FCSTD DOCUMENT  (FreeCAD 0.18R14220 (Git))
Label: sketch_objectsFV7g6h
License: All rights reserved
LicenseURL: http://en.wikipedia.org/wiki/All_rights_reserved
objects: Sketcher::SketchObject×1
note: 1 computed .brp shape members not serialized (recipe doc carries the construction recipe); baked Part::Feature solids carry a one-line shape summary decoded from their .brp

FEATURE [Sketcher::SketchObject] Sketch_sketch_objects
  sketch-geometry (52):
    g0: ArcOfEllipse CenterX=49.7013 CenterY=238.606 CenterZ=0 NormalX=0 NormalY=0 NormalZ=1 MajorRadius=43.2012 MinorRadius=14.2179 AngleXU=-0.622367 StartAngle=5.79407 EndAngle=11.4202
    g1: LineSegment StartX=76.7923 StartY=210.947 StartZ=0 EndX=49.7013 EndY=238.606 EndZ=0
    g2: LineSegment StartX=49.7013 StartY=238.606 StartZ=0 EndX=56.6103 EndY=217.704 EndZ=0
    g3: LineSegment [constr] StartX=41.1792 StartY=270.878 StartZ=0 EndX=41.2353 EndY=287.037 EndZ=0
    g4: LineSegment [constr] StartX=41.2353 StartY=287.037 StartZ=0 EndX=49.7121 EndY=279.07 EndZ=0
    g5: LineSegment [constr] StartX=49.7121 StartY=279.07 StartZ=0 EndX=49.656 EndY=262.912 EndZ=0
    g6: LineSegment [constr] StartX=49.656 StartY=262.912 StartZ=0 EndX=41.1792 EndY=270.878 EndZ=0
    g7: LineSegment [constr] StartX=41.1926 StartY=274.753 StartZ=0 EndX=42.6528 EndY=273.38 EndZ=0
    g8: LineSegment [constr] StartX=42.6528 StartY=273.38 StartZ=0 EndX=42.6393 EndY=269.506 EndZ=0
    g9: LineSegment [constr] StartX=41.2218 StartY=283.163 StartZ=0 EndX=42.682 EndY=281.79 EndZ=0
    g10: LineSegment [constr] StartX=42.682 StartY=281.79 StartZ=0 EndX=42.6954 EndY=285.665 EndZ=0
    g11: LineSegment [constr] StartX=49.6987 StartY=275.196 StartZ=0 EndX=48.2385 EndY=276.568 EndZ=0
    g12: LineSegment [constr] StartX=48.2385 StartY=276.568 StartZ=0 EndX=48.252 EndY=280.442 EndZ=0
    g13: LineSegment [constr] StartX=49.6695 StartY=266.786 StartZ=0 EndX=48.2093 EndY=268.158 EndZ=0
    g14: LineSegment [constr] StartX=48.2093 StartY=268.158 StartZ=0 EndX=48.1959 EndY=264.284 EndZ=0
    g15: LineSegment StartX=41.1919 StartY=274.677 StartZ=0 EndX=41.1332 EndY=283.085 EndZ=0
    g16: LineSegment StartX=42.5821 StartY=285.717 StartZ=0 EndX=48.3338 EndY=280.577 EndZ=0
    g17: LineSegment StartX=49.5946 StartY=276.745 StartZ=0 EndX=49.9588 EndY=268.335 EndZ=0
    g18: LineSegment StartX=48.6946 StartY=264.078 StartZ=0 EndX=42.6645 EndY=269.5 EndZ=0
    g19: ArcOfEllipse CenterX=42.6449 CenterY=273.391 CenterZ=0 NormalX=0 NormalY=0 NormalZ=-1 MajorRadius=4.13656 MinorRadius=1.36086 AngleXU=1.43988 StartAngle=3.50878 EndAngle=5.07438
    g20: ArcOfEllipse CenterX=42.5838 CenterY=281.856 CenterZ=0 NormalX=0 NormalY=0 NormalZ=-1 MajorRadius=4.10185 MinorRadius=1.36491 AngleXU=1.44326 StartAngle=5.06155 EndAngle=6.64982
    g21: ArcOfEllipse CenterX=47.7793 CenterY=276.567 CenterZ=0 NormalX=0 NormalY=0 NormalZ=-1 MajorRadius=4.30289 MinorRadius=1.82063 AngleXU=1.53942 StartAngle=0.382777 EndAngle=1.54265
    g22: ArcOfEllipse CenterX=48.8554 CenterY=268.083 CenterZ=0 NormalX=0 NormalY=0 NormalZ=-1 MajorRadius=4.12784 MinorRadius=1.11184 AngleXU=1.54193 StartAngle=1.51729 EndAngle=3.39278
    g23: LineSegment StartX=63.7123 StartY=263.806 StartZ=0 EndX=55.9428 EndY=260.556 EndZ=0
    g24: LineSegment StartX=55.9428 StartY=260.556 StartZ=0 EndX=49.7121 EndY=266.499 EndZ=0
    g25: LineSegment StartX=49.7121 StartY=266.499 StartZ=0 EndX=49.7121 EndY=277.16 EndZ=0
    g26: LineSegment StartX=49.7121 StartY=277.16 StartZ=0 EndX=55.9428 EndY=284.511 EndZ=0
    g27: LineSegment StartX=55.9428 StartY=284.511 StartZ=0 EndX=63.7123 EndY=283.017 EndZ=0
    g28: LineSegment StartX=63.7123 StartY=283.017 StartZ=0 EndX=67.17 EndY=273.802 EndZ=0
    g29: LineSegment StartX=67.17 StartY=273.802 StartZ=0 EndX=63.7123 EndY=263.806 EndZ=0
    g30: LineSegment StartX=38.4028 StartY=255.231 StartZ=0 EndX=49.656 EndY=262.912 EndZ=0
    g31: LineSegment StartX=49.656 StartY=262.912 StartZ=0 EndX=49.7121 EndY=253.933 EndZ=0
    g32: LineSegment StartX=49.7121 StartY=253.933 StartZ=0 EndX=60.2819 EndY=256.396 EndZ=0
    g33: BSplineCurve PolesCount=4 KnotsCount=2 Degree=3 IsPeriodic=0
    g34: Circle [constr] CenterX=49.7121 CenterY=300.956 CenterZ=0 NormalX=0 NormalY=0 NormalZ=1 AngleXU=0 Radius=0.72
    g35: Circle [constr] CenterX=60.1938 CenterY=311.107 CenterZ=0 NormalX=0 NormalY=0 NormalZ=1 AngleXU=0 Radius=0.72
    g36: Circle [constr] CenterX=60.5017 CenterY=302.786 CenterZ=0 NormalX=0 NormalY=0 NormalZ=1 AngleXU=0 Radius=0.72
    g37: BSplineCurve PolesCount=4 KnotsCount=2 Degree=3 IsPeriodic=0
    g38: Circle [constr] CenterX=60.8097 CenterY=294.464 CenterZ=0 NormalX=0 NormalY=0 NormalZ=1 AngleXU=0 Radius=0.72
    g39: Circle [constr] CenterX=58.9652 CenterY=288.321 CenterZ=0 NormalX=0 NormalY=0 NormalZ=1 AngleXU=0 Radius=0.72
    g40: Circle [constr] CenterX=52.8356 CenterY=284.504 CenterZ=0 NormalX=0 NormalY=0 NormalZ=1 AngleXU=0 Radius=0.72
    g41: BSplineCurve PolesCount=4 KnotsCount=2 Degree=3 IsPeriodic=0
    g42: Circle [constr] CenterX=46.7061 CenterY=280.688 CenterZ=0 NormalX=0 NormalY=0 NormalZ=1 AngleXU=0 Radius=0.72
    g43: Circle [constr] CenterX=41.9049 CenterY=288.11 CenterZ=0 NormalX=0 NormalY=0 NormalZ=1 AngleXU=0 Radius=0.72
    g44: Circle [constr] CenterX=47.8785 CenterY=292.399 CenterZ=0 NormalX=0 NormalY=0 NormalZ=1 AngleXU=0 Radius=0.72
    g45: BSplineCurve PolesCount=4 KnotsCount=2 Degree=3 IsPeriodic=0
    g46: Circle [constr] CenterX=53.8521 CenterY=296.689 CenterZ=0 NormalX=0 NormalY=0 NormalZ=1 AngleXU=0 Radius=0.72
    g47: Circle [constr] CenterX=56.7703 CenterY=298.754 CenterZ=0 NormalX=0 NormalY=0 NormalZ=1 AngleXU=0 Radius=0.72
    g48: Circle [constr] CenterX=54.8429 CenterY=293.355 CenterZ=0 NormalX=0 NormalY=0 NormalZ=1 AngleXU=0 Radius=0.72
    g49: BSplineCurve PolesCount=4 KnotsCount=2 Degree=3 IsPeriodic=0
    g50: Circle [constr] CenterX=52.9156 CenterY=287.956 CenterZ=0 NormalX=0 NormalY=0 NormalZ=1 AngleXU=0 Radius=0.72
    g51: Circle [constr] CenterX=49.7121 CenterY=287.987 CenterZ=0 NormalX=0 NormalY=0 NormalZ=1 AngleXU=0 Radius=0.72
  constraints (87):
    c: Coincident(g0,g1)
    c: Coincident(g2,g0)
    c: Coincident(g1,g2)
    c: Coincident(g1,g0)
    c: Coincident(g3,g4)
    c: Coincident(g4,g5)
    c: Coincident(g5,g6)
    c: Coincident(g6,g3)
    c: Coincident(g7,g8)
    c: Coincident(g9,g10)
    c: Coincident(g11,g12)
    c: Coincident(g13,g14)
    c: Equal(g7,g9)
    c: Equal(g7,g11)
    c: Equal(g7,g13)
    c: Equal(g8,g10)
    c: Equal(g8,g12)
    c: Equal(g8,g14)
    c: PointOnObject(g7,g3)
    c: PointOnObject(g8,g6)
    c: PointOnObject(g9,g3)
    c: PointOnObject(g10,g4)
    c: PointOnObject(g11,g5)
    c: PointOnObject(g12,g4)
    c: PointOnObject(g13,g5)
    c: PointOnObject(g14,g6)
    c: Parallel(g3,g5)
    c: Parallel(g3,g8)
    c: Parallel(g3,g10)
    c: Parallel(g3,g12)
    c: Parallel(g3,g14)
    c: Parallel(g4,g6)
    c: Parallel(g4,g7)
    c: Parallel(g4,g9)
    c: Parallel(g4,g11)
    c: Parallel(g4,g13)
    c: Tangent(g19,g15) = 1.5708
    c: Tangent(g15,g20) = 1.5708
    c: Tangent(g20,g16) = 1.5708
    c: Tangent(g16,g21) = 1.5708
    c: Tangent(g21,g17) = 1.5708
    c: Tangent(g17,g22) = 1.5708
    c: Tangent(g22,g18) = 1.5708
    c: Tangent(g18,g19) = 1.5708
    c: Coincident(g23,g24)
    c: Coincident(g24,g25)
    c: Coincident(g25,g26)
    c: Coincident(g26,g27)
    c: Coincident(g27,g28)
    c: Coincident(g28,g29)
    c: Coincident(g29,g23)
    c: Coincident(g30,g31)
    c: Coincident(g31,g32)
    c: Radius(g34) = 0.72
    c: Equal(g35,g34)
    c: Equal(g36,g34)
    c: InternalAlignment(g34,g33)
    c: InternalAlignment(g34,g33)
    c: InternalAlignment(g35,g33)
    c: InternalAlignment(g36,g33)
    c: Equal(g38,g34)
    c: Equal(g39,g34)
    c: Equal(g40,g34)
    c: InternalAlignment(g36,g37)
    c: InternalAlignment(g38,g37)
    c: InternalAlignment(g39,g37)
    c: InternalAlignment(g40,g37)
    c: Equal(g42,g34)
    c: Equal(g43,g34)
    c: Equal(g44,g34)
    c: InternalAlignment(g40,g41)
    c: InternalAlignment(g42,g41)
    c: InternalAlignment(g43,g41)
    c: InternalAlignment(g44,g41)
    c: Equal(g46,g34)
    c: Equal(g47,g34)
    c: Equal(g48,g34)
    c: InternalAlignment(g44,g45)
    c: InternalAlignment(g46,g45)
    c: InternalAlignment(g47,g45)
    c: InternalAlignment(g48,g45)
    c: Equal(g50,g34)
    c: Equal(g51,g34)
    c: InternalAlignment(g48,g49)
    c: InternalAlignment(g50,g49)
    c: InternalAlignment(g51,g49)
    c: InternalAlignment(g51,g49)
